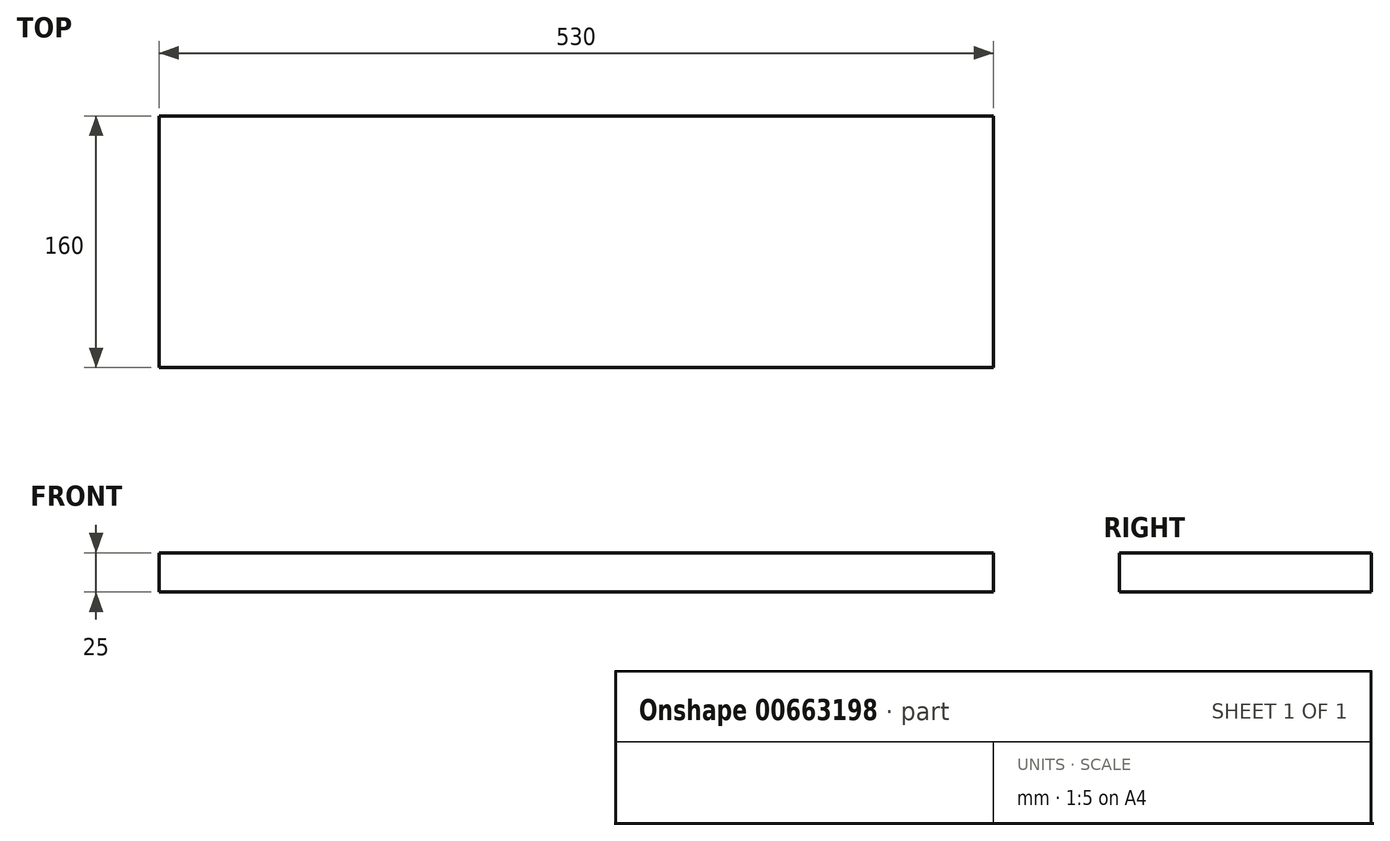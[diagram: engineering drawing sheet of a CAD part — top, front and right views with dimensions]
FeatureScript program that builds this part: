
annotation { "Feature Type Name" : "Feature", "Feature Type Description" : "" }
export const myFeature = defineFeature(function(context is Context, id is Id, definition is map)
    precondition{}
    {
        {
            var Q0;
            Q0=qCreatedBy(makeId("Top.planeOp"),FACE);
            var sketch = newSketch(context, id + "F0", { "sketchPlane" : qUnion([Q0])});
            skLineSegment(sketch, "E0.bottom", {"start": v(-265, 80) * mm, "end": v(265, 80) * mm});
            skLineSegment(sketch, "E0.top", {"start": v(-265, -80) * mm, "end": v(265, -80) * mm});
            skLineSegment(sketch, "E0.left", {"start": v(-265, 80) * mm, "end": v(-265, -80) * mm});
            skLineSegment(sketch, "E0.right", {"start": v(265, 80) * mm, "end": v(265, -80) * mm});
            skPoint(sketch, "E0.middle", {"position": v(0, 0) * mm});
            skSolve(sketch);
        }
        {
            var Q0;
            Q0 = qSketchRegion(id + "F0", true);
            extrude(context, id + "F1", {"entities" : qUnion([Q0]), "endBound" : BoundingType.SYMMETRIC, "depth" : 25 * mm, "offsetDistance" : 25 * mm});
        }
    });
